# Revit family: Pulsadores_Aguilera Electronica
name_source: partatom
category: Dispositivos de alarma de incendios
revit_build: Autodesk Revit 2017 (Build: 20160225_1515(x64)
units: mm (PartAtom-declared; Revit-internal decimal feet)

## family parameters
Anfitrión = Cara
Compartido = No
Corte con vacíos al cargar = No
Cota de conector redondo = Diámetro de uso
Mantener orientación de anotación = Sí
Número OmniClass = 23.85.30.21.11.17
Punto de cálculo de habitación = No
Tipo de pieza = Normal
Título OmniClass = Other Components

## types (5) — shared parameters
Ancho = 98 mm  [stored 0.321522 ft]
Elevación por defecto = 1200 mm
Fabricante = Aguilera Electrónica
Simbolo = Sí
Simbolo texto modelo = Sí
Tapa metacrilato = Plástico, transparente
URL = https://aguilera.es
zero-valued in all types: Costo

## per-type parameters (varying)
| type | Alto | Carcasa | Comentarios de tipo | Descripción | Fondo hueco | Hueco | Llave | Luz indicador | Modelo | Nota clave | Profundidad | Profundidad tapa | Protector ext. | Protector int. | Señales | Tapa metacrilato protección |
| Pulsador de alarma con autochequeo | 95 mm | Plástico ABS rojo | Desarrollado y fabricado por Aguilera Electrónica según Norma EN 54-11.

Equipado con: Microrruptor, led de alarma y autochequeo, sistema de comprobación con llave de rearme, lámina de plástico calibrada para que se enclave y no se rompa.

Pulsador tapa de protección.
Ubicado en caja ABS.
Certificado CE emitido por LPCB.
Dimensiones: 98 X95X39mm | Pulsador manual de alarma desarrollado y fabricado según norma UNE EN 54-11:2001, para su conexión en bucles de detección convencionales. Este equipo está indicado para su instalación en el interior de los locales, para que los usuarios puedan avisar precozmente de un incendio. De esta forma, permite actuar cuando el efecto del incendio está en su fase inicial. Incorpora una tapa de protección transparente para evitar activaciones accidentales. El diseño del pulsador permite activarlo sin que se rompa la lámina de presión, pudiendo rearmarlo nuevamente introduciendo la llave de rearme por un lateral. Ubicado en caja de ABS de color rojo con medidas y serigrafía según normas. | 36 mm  [stored 0.11811 ft] | 35 mm  [stored 0.114829 ft] | No | Sí | AE/V-PSAT |  | 39 mm | 41 mm | 38 mm | 37 mm | 37 mm | No |
| Pulsador de bloqueo de extinción | 98 mm  [stored 0.321522 ft] | Plástico ABS azul | Pulsador diseñado según norma EN12094-3 para bloquear el disparo de un sistema de extinción. Color azul. Uso interior. Serigrafiado con el texto PARO EXTINCIÓN.
Equipado con: Microrruptor, sistema de comprobación con llave de rearme, tapa de protección de metacrilato transparente, contactos normalmente abierto NA, común C y normalmente cerrado NC y lámina de plástico calibrada para que se enclave y no rompa.

Ubicado en caja ABS de 98X98X50 mm | Pulsador diseñado para bloquear el disparo de un sistema de extinción. Color
azul. Uso interior. Serigrafiado con el texto PARO EXTINCIÓN.
Equipado con: Microrruptor, sistema de comprobación con llave de rearme, tapa
de protección de metacrilato transparente, contactos normalmente abierto NA,
común C y normalmente cerrado NC y lámina de plástico calibrada para que se
enclave y no rompa.
Ubicado en caja ABS de 98X98X50 mm | 47 mm | 46 mm | Sí | No | AE/V-PB2 |  | 50 mm  [stored 0.164042 ft] | 52 mm | 49 mm  [stored 0.160761 ft] | 48 mm  [stored 0.15748 ft] | 48 mm  [stored 0.15748 ft] | Sí |
| Pulsador de disparo de extinción | 98 mm  [stored 0.321522 ft] | Plástico ABS amarillo | Pulsador diseñado según norma EN12094-3 para provocar el disparo de un sistema de extinción. Color amarillo. Uso interior. Serigrafiado con el texto DISPARO EXTINCIÓN.

Equipado con: Microrruptor, sistema de comprobación con llave de rearme, tapa de protección de metacrilato transparente, contactos normalmente abierto NA, común C y normalmente cerrado NC y lámina de plástico calibrada para que se enclave y no rompa.

Ubicado en caja ABS de 98X98X50 mm | Pulsador diseñado para provocar el disparo de un sistema de extinción. Color
amarillo. Uso interior. Serigrafiado con el texto DISPARO EXTINCIÓN.
Equipado con: Microrruptor, sistema de comprobación con llave de rearme, tapa de
protección de metacrilato transparente, contactos normalmente abierto NA, común
C y normalmente cerrado NC y lámina de plástico calibrada para que se enclave y
no rompa.
Ubicado en caja ABS de 98X98X50 mm | 47 mm | 46 mm | Sí | No | AE/V-PD2 | Pulsador de disparo de extinción | 50 mm  [stored 0.164042 ft] | 52 mm | 49 mm  [stored 0.160761 ft] | 48 mm  [stored 0.15748 ft] | 48 mm  [stored 0.15748 ft] | Sí |
| Pulsador de emergencia | 98 mm  [stored 0.321522 ft] | Plástico ABS verde | Pulsador de evacuación diseñado para su instalación en salidas de emergencia.

Color verde. Uso interior.

Equipado con: Microrruptor, sistema de comprobación con llave de rearme,tapa de protección de metacrilato transparente, contactos normalmente abierto NA, común C y normalmente cerrado NC y lámina de plástico calibrada para que se enclave y no rompa.

Ubicado en caja ABS de 98X98X50 mm. | Pulsador de evacuación diseñado para su instalación en salidas de emergencia.

Color verde. Uso interior.

Equipado con: Microrruptor, sistema de comprobación con llave de rearme,tapa de protección de metacrilato transparente, contactos normalmente abierto NA, común C y normalmente cerrado NC y lámina de plástico calibrada para que se enclave y no rompa.

Ubicado en caja ABS de 98X98X50 mm. | 47 mm | 46 mm | Sí | No | AE/V-PE |  | 50 mm  [stored 0.164042 ft] | 52 mm | 49 mm  [stored 0.160761 ft] | 48 mm  [stored 0.15748 ft] | 48 mm  [stored 0.15748 ft] | Sí |
| Pulsador de alarma para exterior | 95 mm | Plástico ABS rojo | Pulsador de alarma convencional indicado para uso en exterior, IP65 según norma EN 54-11. Dispone de microrruptor con resistencia de carga de 470 ohm o de 680 ohm, sistema de comprobación con llave de rearme y led de alarma.

Permite el montaje de lámina de plástico calibrada para que se enclave y no se rompa o de cristal rompible ambos sumunistrados. Caja ABS 85x85x58 mm. Certificado CE según DPC. Certificado LPCB.

Protección: IP 65 | Pulsador de alarma convencional indicado para uso en exterior, IP65 según norma EN 54-11. Dispone de microrruptor con resistencia de carga de 470 ohm o de 680 ohm, sistema de comprobación con llave de rearme y led de alarma. Permite el montaje de lámina de plástico calibrada para que se enclave y no rompa o de cristal rompible -ambos suministrados.
Caja ABS 85x85x58 mm
Certificado CE según DPC. Certificado LPCB. | 36 mm  [stored 0.11811 ft] | 35 mm  [stored 0.114829 ft] | No | Sí | AE/V-PSIP |  | 39 mm | 41 mm | 38 mm | 37 mm | 37 mm | No |

note: [stored X ft] marks values corroborated as IEEE doubles in the binary element streams (Revit-internal decimal feet)
